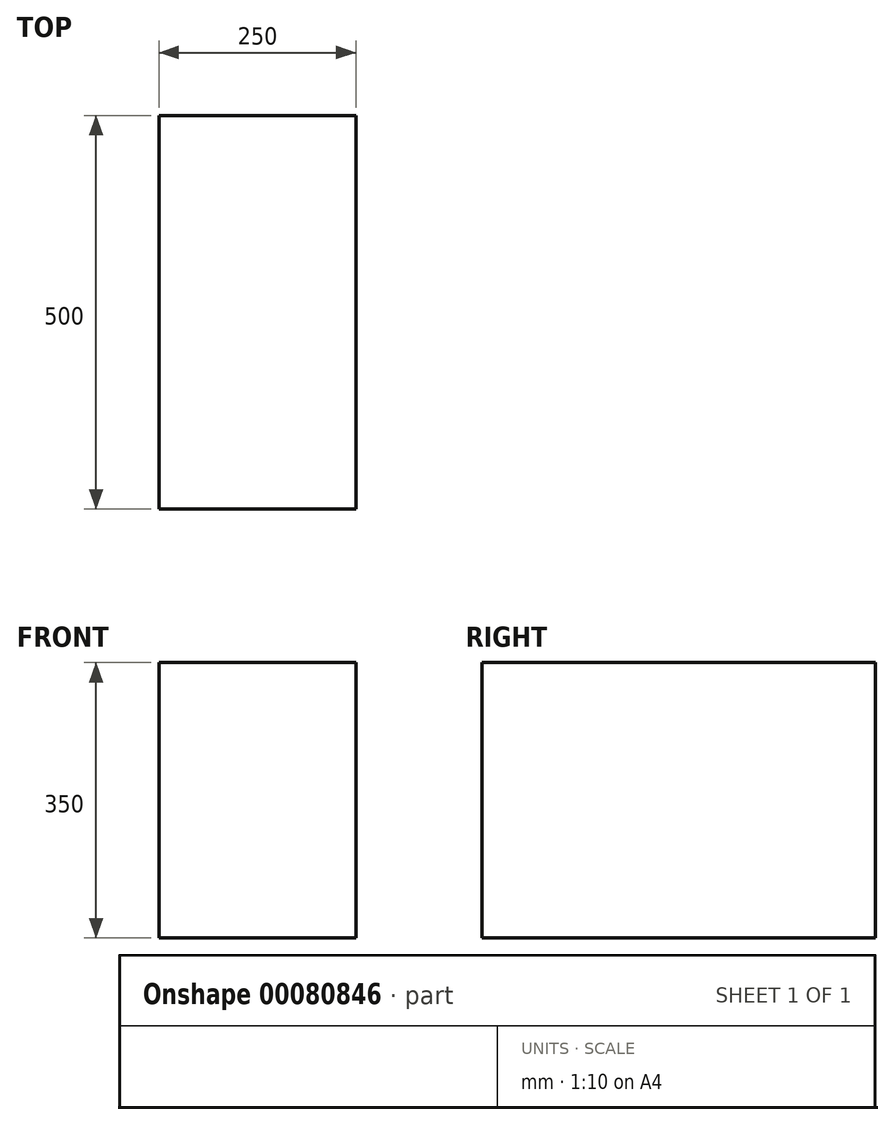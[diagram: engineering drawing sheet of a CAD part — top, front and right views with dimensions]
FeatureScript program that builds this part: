
annotation { "Feature Type Name" : "Feature", "Feature Type Description" : "" }
export const myFeature = defineFeature(function(context is Context, id is Id, definition is map)
    precondition{}
    {
        {
            var Q0;
            Q0=qCreatedBy(makeId("Top.planeOp"),FACE);
            var sketch = newSketch(context, id + "F0", { "sketchPlane" : qUnion([Q0])});
            skLineSegment(sketch, "E0.bottom", {"start": v(-125, 250) * mm, "end": v(125, 250) * mm});
            skLineSegment(sketch, "E0.top", {"start": v(-125, -250) * mm, "end": v(125, -250) * mm});
            skLineSegment(sketch, "E0.left", {"start": v(-125, 250) * mm, "end": v(-125, -250) * mm});
            skLineSegment(sketch, "E0.right", {"start": v(125, 250) * mm, "end": v(125, -250) * mm});
            skPoint(sketch, "E0.middle", {"position": v(0, 0) * mm});
            skSolve(sketch);
        }
        {
            var Q0;
            Q0=makeQuery(id+"F0.imprint","IMPRINT",FACE,{"disambiguationData":[TD([[makeQuery(id+"F0.imprint","IMPRINT",EDGE,{"derivedFrom":sQuery(id+"F0.wireOp",EDGE,"E0.bottom")}),-1.0]])]});
            extrude(context, id + "F1", {"entities" : qUnion([Q0]), "depth" : 350 * mm});
        }
    });
